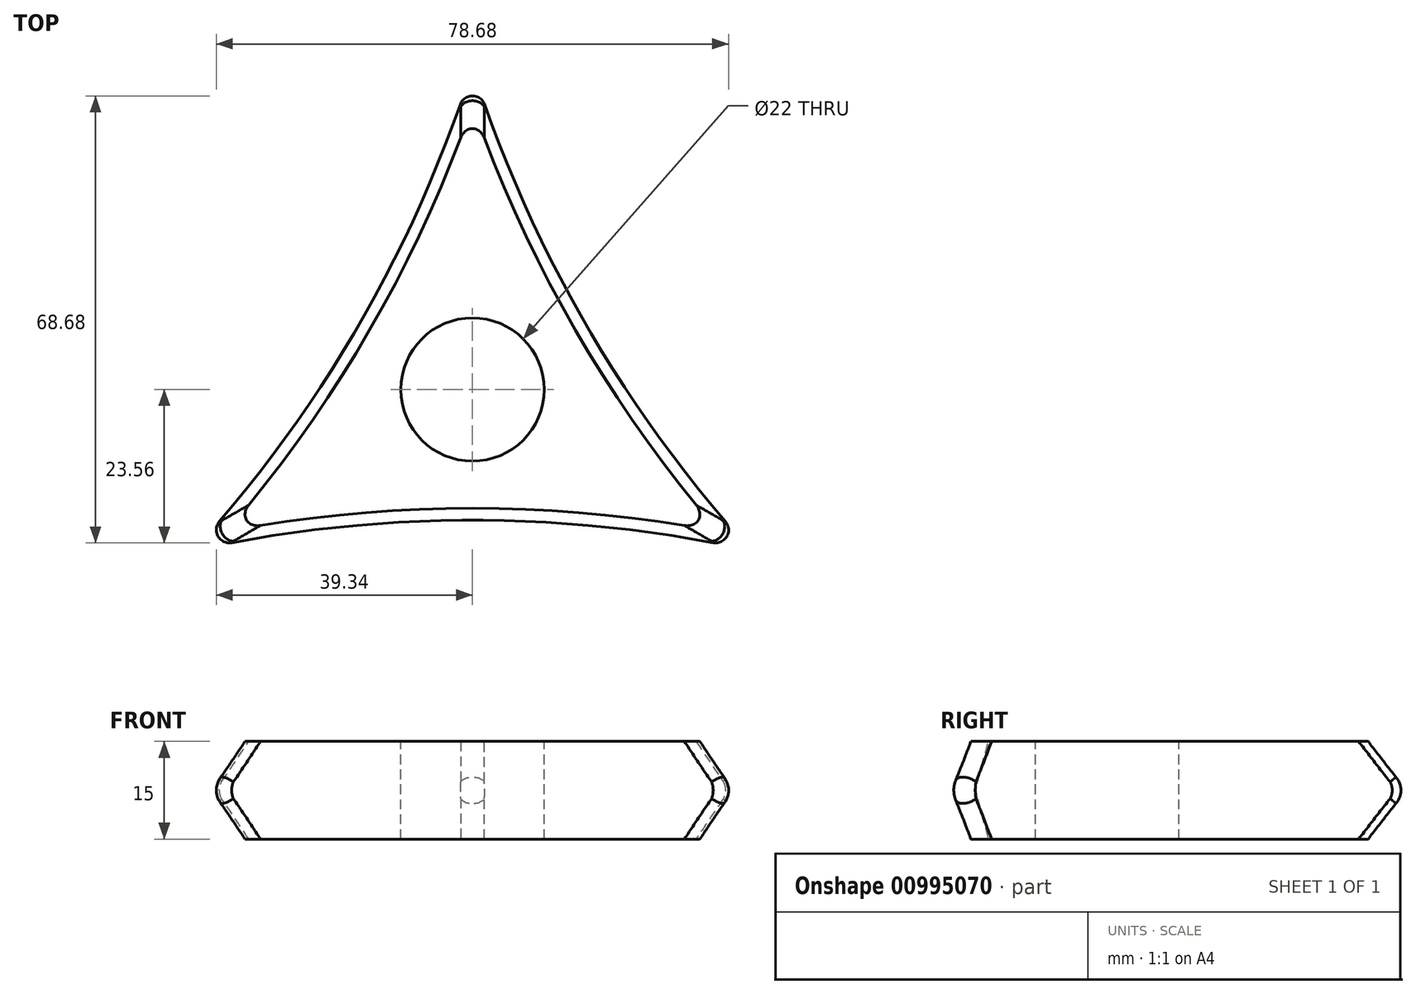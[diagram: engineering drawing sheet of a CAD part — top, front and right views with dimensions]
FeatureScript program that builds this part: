
annotation { "Feature Type Name" : "Feature", "Feature Type Description" : "" }
export const myFeature = defineFeature(function(context is Context, id is Id, definition is map)
    precondition{}
    {
        {
            var Q0;
            Q0=qCreatedBy(makeId("Top.planeOp"),FACE);
            var sketch = newSketch(context, id + "F0", { "sketchPlane" : qUnion([Q0])});
            skCircle(sketch, "E0", {"center": v(0, 0) * mm, "radius": 7.5 * mm, "construction": true});
            skCircle(sketch, "E1", {"center": v(0, 0) * mm, "radius": 50 * mm, "construction": true});
            skLineSegment(sketch, "E2", {"start": v(0, 50) * mm, "end": v(-43.3, -25) * mm, "construction": true});
            skLineSegment(sketch, "E3", {"start": v(-43.3, -25) * mm, "end": v(43.3, -25) * mm, "construction": true});
            skLineSegment(sketch, "E4", {"start": v(43.3, -25) * mm, "end": v(0, 50) * mm, "construction": true});
            skArc(sketch, "E5", {"start": v(43.3, -25) * mm, "mid": v(0, -20.26) * mm, "end": v(-43.3, -25) * mm});
            skArc(sketch, "E6", {"start": v(-43.3, -25) * mm, "mid": v(-17.54, 10.13) * mm, "end": v(0, 50) * mm});
            skArc(sketch, "E7", {"start": v(0, 50) * mm, "mid": v(17.54, 10.13) * mm, "end": v(43.3, -25) * mm});
            skSolve(sketch);
        }
        {
            var Q0;
            Q0=qCreatedBy(makeId("Top.planeOp"),FACE);
            var sketch = newSketch(context, id + "F1", { "sketchPlane" : qUnion([Q0])});
            skCircle(sketch, "E8", {"center": v(0, 0) * mm, "radius": 11 * mm});
            skSolve(sketch);
        }
        {
            var Q0;
            Q0 = qSketchRegion(id + "F0", true);
            extrude(context, id + "F2", {"entities" : qUnion([Q0]), "endBound" : BoundingType.SYMMETRIC, "depth" : 15 * mm, "offsetDistance" : 25 * mm, "hasDraft" : true, "draftAngle" : 15 * degree, "draftPullDirection" : true});
        }
        {
            var Q0;
            Q0=makeQuery(id+"F2.opExtrude","CAP_FACE",FACE,{"disambiguationData":[OSD([sQuery(id+"F0.wireOp",EDGE,"E5"),sQuery(id+"F0.wireOp",EDGE,"E6"),sQuery(id+"F0.wireOp",EDGE,"E7")])],"isStart":false});
            var sketch = newSketch(context, id + "F3", { "sketchPlane" : qUnion([Q0])});
            skPoint(sketch, "E9", {"position": v(0, 0) * mm});
            skSolve(sketch);
        }
        {
            var Q0;
            Q0=sQuery(id+"F3.wireOp",VERTEX,"E9");
            var Q1;
            Q1=makeQuery(id+"F2.*.split.splitOp","SPLIT",BODY,{"derivedFrom":makeQuery(id+"F2.opExtrude","SWEPT_BODY",BODY,{"disambiguationData":[OSD([sQuery(id+"F0.wireOp",EDGE,"E5"),sQuery(id+"F0.wireOp",EDGE,"E6"),sQuery(id+"F0.wireOp",EDGE,"E7")])]})});
            hole(context, id + "F4", {"style" : HoleStyle.SIMPLE, "endStyle" : HoleEndStyle.THROUGH, "holeDiameter" : 22 * mm, "majorDiameter" : 5 * mm, "isTappedThrough" : true, "tappedDepth" : 12 * mm, "tapClearance" : 3, "locations" : qUnion([Q0]), "scope" : qUnion([Q1])});
        }
        {
            var Q0;
            {var subQ0=makeQuery(id+"F2.opExtrude","SWEPT_FACE",FACE,{"disambiguationData":[OSD([sQuery(id+"F0.wireOp",EDGE,"E5")])]});Q0=makeQuery(id+"F2.*.booleanUnion.opBoolean","MERGE",EDGE,{"derivedFrom":[makeQuery(id+"F2.*.split.splitOp","SPLIT_SURFACE_INTERSECT",EDGE,{"derivedFrom":[subQ0]}),makeQuery(id+"F2.*.split.splitOp","SPLIT_SURFACE_INTERSECT",EDGE,{"derivedFrom":[subQ0],"isFromBackBody":true})]});}
            var Q1;
            {var subQ0=makeQuery(id+"F2.opExtrude","SWEPT_FACE",FACE,{"disambiguationData":[OSD([sQuery(id+"F0.wireOp",EDGE,"E7")])]});Q1=makeQuery(id+"F2.*.booleanUnion.opBoolean","MERGE",EDGE,{"derivedFrom":[makeQuery(id+"F2.*.split.splitOp","SPLIT_SURFACE_INTERSECT",EDGE,{"derivedFrom":[subQ0]}),makeQuery(id+"F2.*.split.splitOp","SPLIT_SURFACE_INTERSECT",EDGE,{"derivedFrom":[subQ0],"isFromBackBody":true})]});}
            var Q2;
            {var subQ0=makeQuery(id+"F2.opExtrude","SWEPT_FACE",FACE,{"disambiguationData":[OSD([sQuery(id+"F0.wireOp",EDGE,"E6")])]});Q2=makeQuery(id+"F2.*.booleanUnion.opBoolean","MERGE",EDGE,{"derivedFrom":[makeQuery(id+"F2.*.split.splitOp","SPLIT_SURFACE_INTERSECT",EDGE,{"derivedFrom":[subQ0]}),makeQuery(id+"F2.*.split.splitOp","SPLIT_SURFACE_INTERSECT",EDGE,{"derivedFrom":[subQ0],"isFromBackBody":true})]});}
            fillet(context, id + "F5", {"entities" : qUnion([Q0, Q1, Q2]), "radius" : 5 * mm, "tangentPropagation" : true, "allowEdgeOverflow" : false});
        }
        {
            var Q0;
            Q0=makeQuery(id+"F2.*.split.splitOp","SPLIT",EDGE,{"derivedFrom":makeQuery(id+"F2.opExtrude","SWEPT_EDGE",EDGE,{"disambiguationData":[OSD([sQuery(id+"F0.wireOp",EDGE,"E5"),sQuery(id+"F0.wireOp",EDGE,"E6")])]})});
            var Q1;
            Q1=makeQuery(id+"F2.*.split.splitOp","SPLIT",EDGE,{"derivedFrom":makeQuery(id+"F2.opExtrude","SWEPT_EDGE",EDGE,{"disambiguationData":[OSD([sQuery(id+"F0.wireOp",EDGE,"E5"),sQuery(id+"F0.wireOp",EDGE,"E7")])]})});
            var Q2;
            Q2=makeQuery(id+"F2.*.split.splitOp","SPLIT",EDGE,{"derivedFrom":makeQuery(id+"F2.opExtrude","SWEPT_EDGE",EDGE,{"disambiguationData":[OSD([sQuery(id+"F0.wireOp",EDGE,"E6"),sQuery(id+"F0.wireOp",EDGE,"E7")])]})});
            fillet(context, id + "F6", {"entities" : qUnion([Q0, Q1, Q2]), "radius" : 2 * mm, "tangentPropagation" : true, "allowEdgeOverflow" : false});
        }
    });
